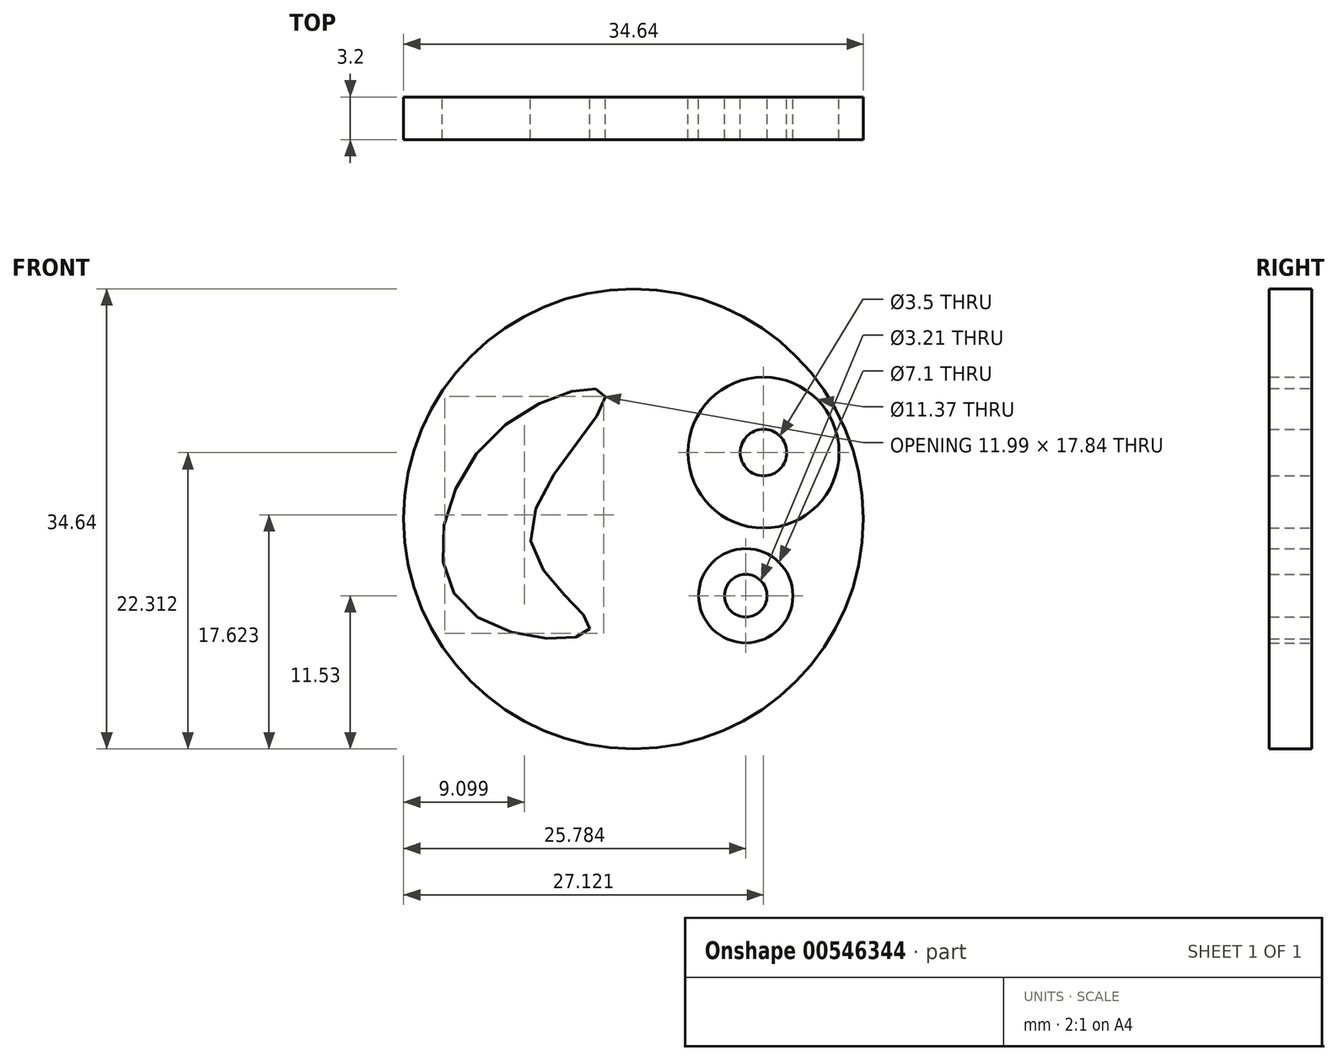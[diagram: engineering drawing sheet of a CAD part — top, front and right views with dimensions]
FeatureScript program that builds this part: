
annotation { "Feature Type Name" : "Feature", "Feature Type Description" : "" }
export const myFeature = defineFeature(function(context is Context, id is Id, definition is map)
    precondition{}
    {
        {
            var Q0;
            Q0=qCreatedBy(makeId("Front.planeOp"),FACE);
            var sketch = newSketch(context, id + "F0", { "sketchPlane" : qUnion([Q0])});
            skCircle(sketch, "E0", {"center": v(-29.57, -40.39) * mm, "radius": 17.32 * mm});
            skCircle(sketch, "E1", {"center": v(-21.1, -46.18) * mm, "radius": 3.55 * mm});
            skCircle(sketch, "E2", {"center": v(-19.77, -35.4) * mm, "radius": 5.69 * mm});
            skCircle(sketch, "E3", {"center": v(-21.1, -46.18) * mm, "radius": 1.6 * mm});
            skCircle(sketch, "E4", {"center": v(-19.77, -35.4) * mm, "radius": 1.75 * mm});
            skFitSpline(sketch, "E5", {"points": [v(-32.87, -48.67) * mm, v(-37.32, -41.81) * mm, v(-31.7, -31.12) * mm, v(-40.09, -34.06) * mm, v(-42.14, -47.16) * mm, v(-32.87, -48.67) * mm]});
            skSolve(sketch);
        }
        {
            var Q0;
            Q0=makeQuery(id+"F0.imprint","IMPRINT",FACE,{"disambiguationData":[TD([[makeQuery(id+"F0.imprint","IMPRINT",EDGE,{"derivedFrom":sQuery(id+"F0.wireOp",EDGE,"E0")}),1.0]])]});
            extrude(context, id + "F1", {"entities" : qUnion([Q0]), "depth" : 3.2 * mm, "offsetDistance" : 25 * mm});
        }
        {
            var Q0;
            Q0=makeQuery(id+"F0.imprint","IMPRINT",FACE,{"disambiguationData":[TD([[makeQuery(id+"F0.imprint","IMPRINT",EDGE,{"derivedFrom":sQuery(id+"F0.wireOp",EDGE,"E1")}),1.0]])]});
            var Q1;
            Q1=makeQuery(id+"F0.imprint","IMPRINT",FACE,{"disambiguationData":[TD([[makeQuery(id+"F0.imprint","IMPRINT",EDGE,{"derivedFrom":sQuery(id+"F0.wireOp",EDGE,"E2")}),1.0]])]});
            extrude(context, id + "F2", {"entities" : qUnion([Q0, Q1]), "depth" : 3.2 * mm, "offsetDistance" : 25 * mm});
        }
        {
            var Q0;
            Q0=makeQuery(id+"F0.imprint","IMPRINT",FACE,{"disambiguationData":[TD([[makeQuery(id+"F0.imprint","IMPRINT",EDGE,{"derivedFrom":sQuery(id+"F0.wireOp",EDGE,"E3")}),1.0]])]});
            var Q1;
            Q1=makeQuery(id+"F0.imprint","IMPRINT",FACE,{"disambiguationData":[TD([[makeQuery(id+"F0.imprint","IMPRINT",EDGE,{"derivedFrom":sQuery(id+"F0.wireOp",EDGE,"E4")}),1.0]])]});
            var Q2;
            Q2=makeQuery(id+"F0.imprint","IMPRINT",FACE,{"disambiguationData":[TD([[makeQuery(id+"F0.imprint","IMPRINT",EDGE,{"derivedFrom":sQuery(id+"F0.wireOp",EDGE,"E5")}),1.0]])]});
            extrude(context, id + "F3", {"entities" : qUnion([Q0, Q1, Q2]), "depth" : 3.2 * mm, "offsetDistance" : 25 * mm});
        }
    });
